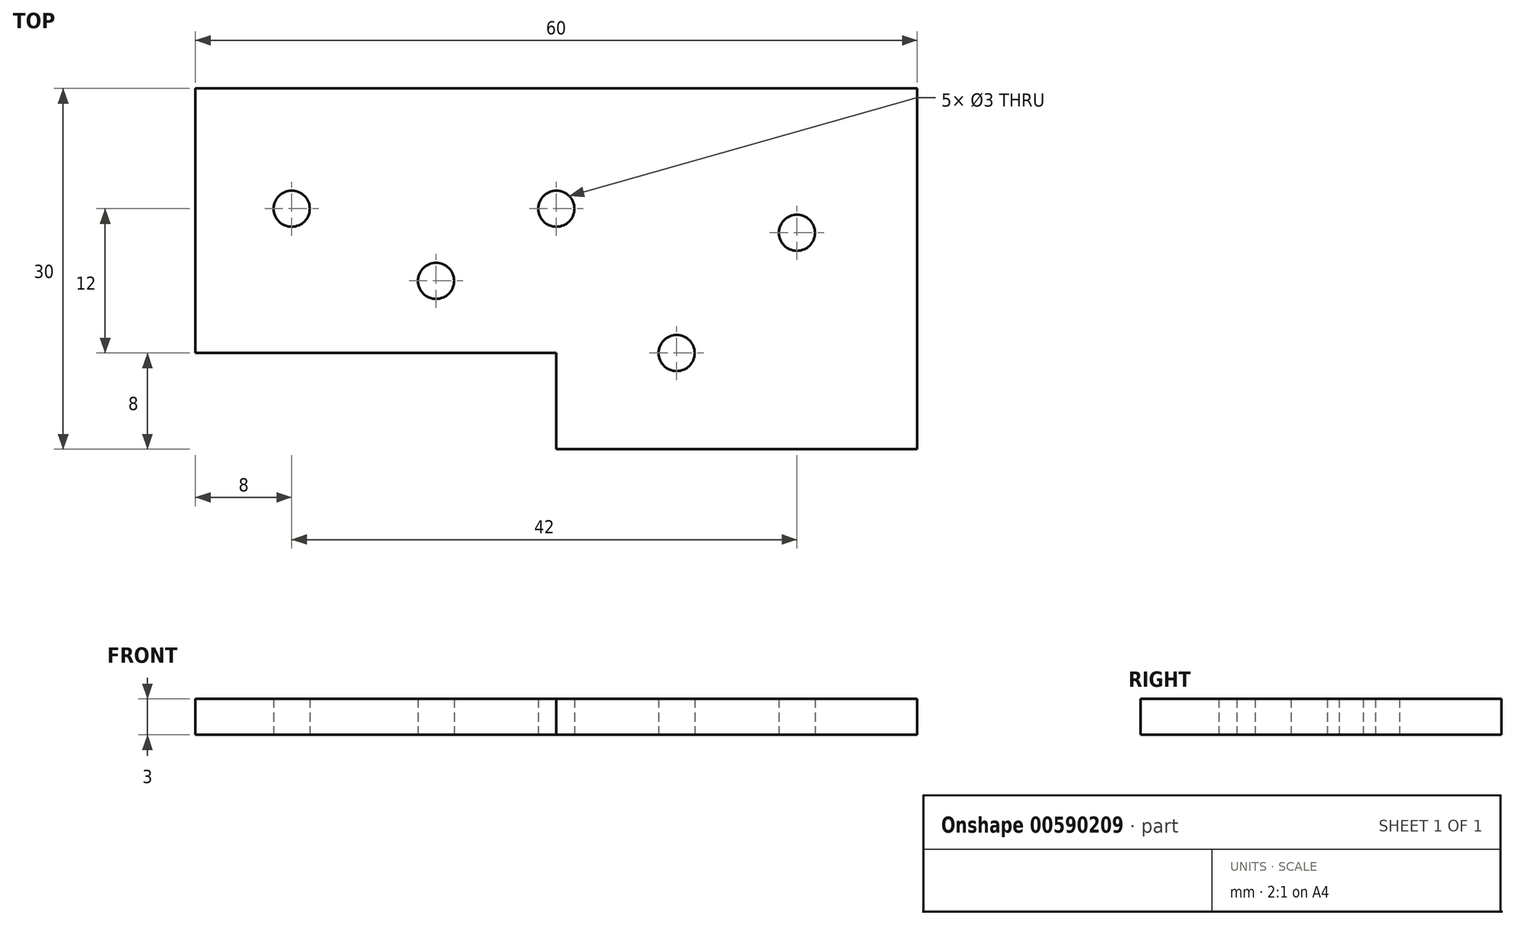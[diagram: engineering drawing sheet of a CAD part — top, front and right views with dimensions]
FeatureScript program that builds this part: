
annotation { "Feature Type Name" : "Feature", "Feature Type Description" : "" }
export const myFeature = defineFeature(function(context is Context, id is Id, definition is map)
    precondition{}
    {
        {
            var Q0;
            Q0=qCreatedBy(makeId("Top.planeOp"),FACE);
            var sketch = newSketch(context, id + "F0", { "sketchPlane" : qUnion([Q0])});
            skLineSegment(sketch, "E0.bottom", {"start": v(-30, 15) * mm, "end": v(30, 15) * mm});
            skLineSegment(sketch, "E0.top", {"start": v(-30, -15) * mm, "end": v(30, -15) * mm});
            skLineSegment(sketch, "E0.left", {"start": v(-30, 15) * mm, "end": v(-30, -15) * mm});
            skLineSegment(sketch, "E0.right", {"start": v(30, 15) * mm, "end": v(30, -15) * mm});
            skPoint(sketch, "E0.middle", {"position": v(0, 0) * mm});
            skLineSegment(sketch, "E1.bottom", {"start": v(-30, -15) * mm, "end": v(0, -15) * mm});
            skLineSegment(sketch, "E1.top", {"start": v(-30, -7) * mm, "end": v(0, -7) * mm});
            skLineSegment(sketch, "E1.left", {"start": v(-30, -15) * mm, "end": v(-30, -7) * mm});
            skLineSegment(sketch, "E1.right", {"start": v(0, -15) * mm, "end": v(0, -7) * mm});
            skCircle(sketch, "E2", {"center": v(-22, 5) * mm, "radius": 1.5 * mm});
            skCircle(sketch, "E3", {"center": v(0, 5) * mm, "radius": 1.5 * mm});
            skCircle(sketch, "E4", {"center": v(20, 3) * mm, "radius": 1.5 * mm});
            skCircle(sketch, "E5", {"center": v(10, -7) * mm, "radius": 1.5 * mm});
            skCircle(sketch, "E6", {"center": v(-10, -1) * mm, "radius": 1.5 * mm});
            skSolve(sketch);
        }
        {
            var Q0;
            Q0=makeQuery(id+"F0.imprint","IMPRINT",FACE,{"disambiguationData":[TD([[makeQuery(id+"F0.imprint","IMPRINT",EDGE,{"derivedFrom":sQuery(id+"F0.wireOp",EDGE,"E0.bottom")}),-1.0]])]});
            extrude(context, id + "F1", {"entities" : qUnion([Q0]), "depth" : 3 * mm, "offsetDistance" : 25 * mm});
        }
    });
